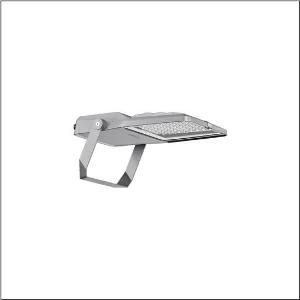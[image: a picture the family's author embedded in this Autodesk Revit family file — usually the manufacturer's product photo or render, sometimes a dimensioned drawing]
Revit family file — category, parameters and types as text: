
# Revit family: floodlight_fl_21_iq_mini___pl64_5xa7771b4e1a_e45f
name_source: partatom
category: Lighting Fixtures
units: mm (PartAtom-declared; Revit-internal decimal feet)

## family parameters
Cut with Voids When Loaded = No
Host = Face
Light Source = No
Part Type = Normal
Room Calculation Point = No
Round Connector Dimension = Use Diameter
Shared = No

## types (1)
- --- (1 x LED, 6270 lm, 45.5 W, 4000K)
    Apparent Load = 46 VA
    CIE Flux Codes = 28 80 98 100 100
    Color Rendering = 70
    Color Temperature = 4000K
    Default Elevation = 1800 mm
    Description = Floodlight FL 21 iQ mini, floodlight, primary light control with lens, of PMMA, primary optical cover: protective disc, of toughened safety glass, transparent, light distribution: PL64, light emission: direct distribution, installation type: surface-mounted, lamps: LED, High Power LED, rated values: 6.270lm | 45,5W | 137,8lm/W (begin service life); end service life: 6.270lm | 48W; at 50% lumin. flux: 3.135lm | 21,5W | 145,8lm/W, colour temperature: 4000K, colour rendering: CRI > 70, light colour: 740, light setting 1 begin service life: 100% | 6.270lm | 45,5W | 137,8lm/W | 4.000K, light setting 1 end service life: 48W, further light settings possible, control: Auto-Match, Temp-Guard, Lumen-Switch, Night-Set, Smart-Wire, Light-Fading, Desk-Remote (wireless, voltage-free reading and setting of iQ features in the workshop via application-optimized NFC function/RFID function), optimised constant luminous flux control (CLO 2.0), pre-setting: linear dimming characteristic, with terminal, 6-pole, mains connection: 220..240V, AC, 50/60Hz, luminaire housing, of diecast aluminium, powder-coated, SITECO metallic grey (DB 702S), corrosivity category C5 mid according to DIN EN ISO 12944suitable for swimming poolschlorine-resistant, sealing non-destructively replaceable, mounting bracket, of steel, galvanised, powder-coated, SITECO metallic grey (DB 702S), protection rating (complete): IP66, insulation class (complete): insulation class II (safety insulation), certification: CE, ENEC, VDE, protection symbol: D, impact resistance: IK08, permissible operating ambient temperature: -40..+40°C, permissible operating ambient temperature for outdoor applications: -40..+50°C, standard: DIN EN 12944, LABS conformity tested according to VDMA 24364:2018-05, packaging unit: 1 piece

Light Distribution: PL64
    Height = 70 mm
    Lamp = 1 x LED
    Lamp Light Flux = 6270 lm
    Lamp Power = 45.5 W
    Lamp count = 1
    Length = 485 mm
    Luminous efficacy = 138 lm/W
    Manufacturer = Siteco
    ModVariant = No
    Model = 5XA7771B4E1A
    Mounting Place = Wall
    Mounting Type = Surface mounted
    Number of Poles = 1
    OnlyDefault = Yes
    Power Factor = 1
    Product Name = Floodlight FL 21 iQ mini | PL64
    Product group = floodlight | wall mounted
    ProductGroupID = 2002
    Protection Class = Protection class II
    Protection Degree = IP 66
    RLX_Detail_Level = 1
    RLX_Emergency_Light_Flux = 0 lm
    RLX_Emergency_Type = 0
    RLX_Emergency_Type_DB = No
    RlxData = <blob elided: 96413 chars, md5=f40f4aba>
    Socket = socket
    Standby Power = 0 W
    System Light Flux = 6270 lm
    System Power = 46 W
    Type Comments = factory setting: luminous flux: 100 % | dim-lin: 254 | 463 mA
    Type Image = l_1006845.jpg
    URL = http://relux.com
    VarID = @adj_168151
    Voltage = 0 V
    Weight = 0.00 kg
    Width = 337 mm

## geometry (parser evidence)
native form markers: Blend x4, Sweep x14
no freeform markers — native parametric forms only
